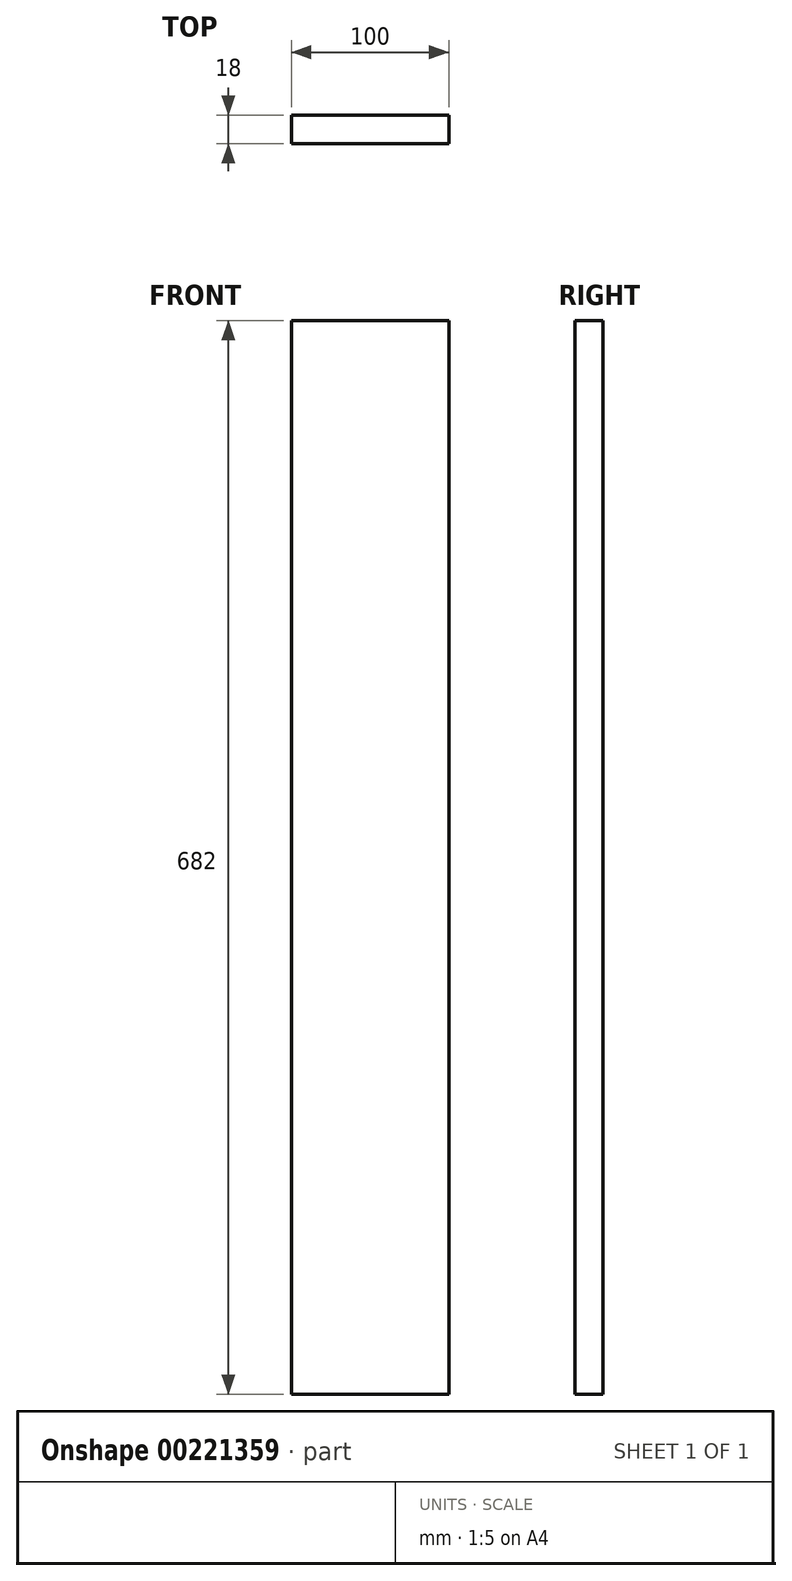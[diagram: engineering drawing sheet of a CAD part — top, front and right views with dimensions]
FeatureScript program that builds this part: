
annotation { "Feature Type Name" : "Feature", "Feature Type Description" : "" }
export const myFeature = defineFeature(function(context is Context, id is Id, definition is map)
    precondition{}
    {
        {
            var Q0;
            Q0=qCreatedBy(makeId("Front.planeOp"),FACE);
            var sketch = newSketch(context, id + "F0", { "sketchPlane" : qUnion([Q0])});
            skLineSegment(sketch, "E0.bottom", {"start": v(50, -341) * mm, "end": v(-50, -341) * mm});
            skLineSegment(sketch, "E0.top", {"start": v(50, 341) * mm, "end": v(-50, 341) * mm});
            skLineSegment(sketch, "E0.left", {"start": v(50, -341) * mm, "end": v(50, 341) * mm});
            skLineSegment(sketch, "E0.right", {"start": v(-50, -341) * mm, "end": v(-50, 341) * mm});
            skPoint(sketch, "E0.middle", {"position": v(0, 0) * mm});
            skSolve(sketch);
        }
        {
            var Q0;
            Q0 = qSketchRegion(id + "F0", true);
            extrude(context, id + "F1", {"entities" : qUnion([Q0]), "depth" : 18 * mm});
        }
    });
